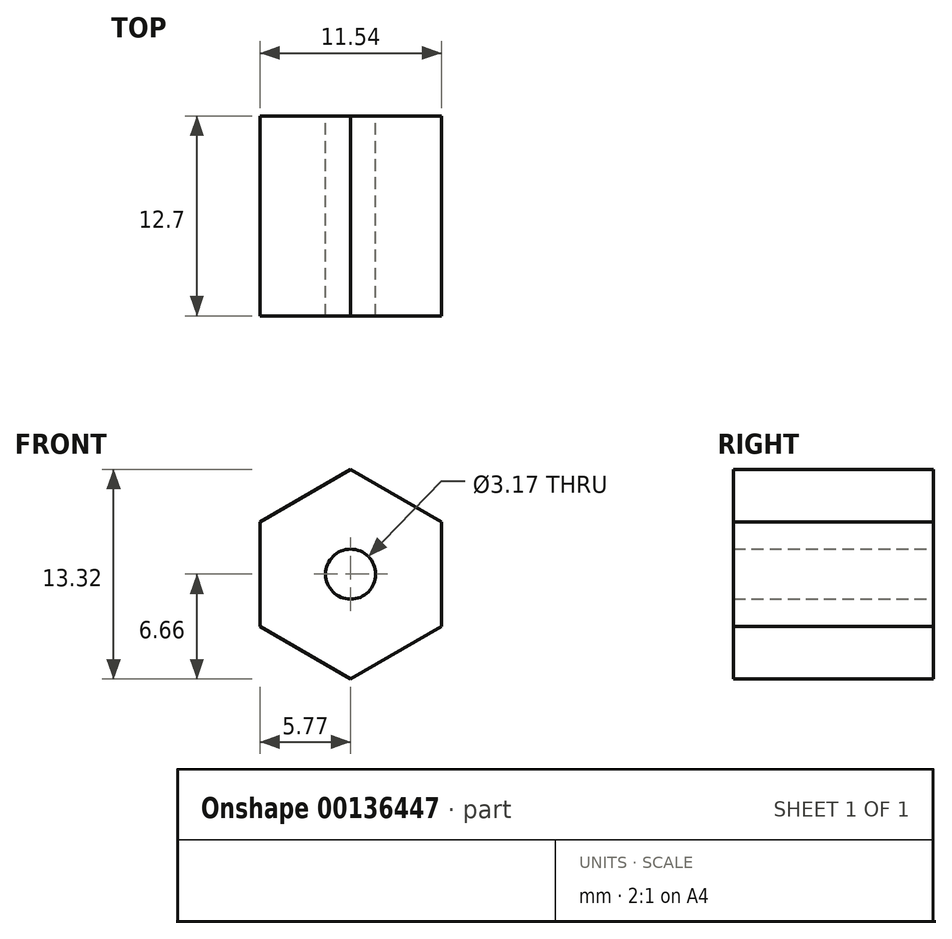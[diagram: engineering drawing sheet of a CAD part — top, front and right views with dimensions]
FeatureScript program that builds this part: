
annotation { "Feature Type Name" : "Feature", "Feature Type Description" : "" }
export const myFeature = defineFeature(function(context is Context, id is Id, definition is map)
    precondition{}
    {
        {
            var Q0;
            Q0=qCreatedBy(makeId("Front.planeOp"),FACE);
            var sketch = newSketch(context, id + "F0", { "sketchPlane" : qUnion([Q0])});
            skLineSegment(sketch, "E0", {"start": v(0, 0) * mm, "end": v(0, 6.66) * mm});
            skPoint(sketch, "E1.center", {"position": v(0, 0) * mm});
            skCircle(sketch, "E2", {"center": v(0, 0) * mm, "radius": 1.59 * mm});
            skLineSegment(sketch, "E3.1.0", {"start": v(0, 0) * mm, "end": v(-1.37, 0.8) * mm});
            skLineSegment(sketch, "E3.2.0", {"start": v(0, 0) * mm, "end": v(-1.37, -0.8) * mm});
            skLineSegment(sketch, "E3.3.0", {"start": v(0, 0) * mm, "end": v(0, -1.59) * mm});
            skLineSegment(sketch, "E3.4.0", {"start": v(0, 0) * mm, "end": v(1.37, -0.8) * mm});
            skLineSegment(sketch, "E3.5.0", {"start": v(0, 0) * mm, "end": v(1.37, 0.8) * mm});
            skLineSegment(sketch, "E4", {"start": v(0, 6.66) * mm, "end": v(-5.77, 3.33) * mm});
            skLineSegment(sketch, "E5", {"start": v(-5.77, -3.33) * mm, "end": v(-5.77, 3.33) * mm});
            skLineSegment(sketch, "E6", {"start": v(-5.77, -3.33) * mm, "end": v(0, -6.66) * mm});
            skLineSegment(sketch, "E7", {"start": v(0, -6.66) * mm, "end": v(5.77, -3.33) * mm});
            skLineSegment(sketch, "E8", {"start": v(5.77, -3.33) * mm, "end": v(5.77, 3.33) * mm});
            skLineSegment(sketch, "E9", {"start": v(5.77, 3.33) * mm, "end": v(0, 6.66) * mm});
            skSolve(sketch);
        }
        {
            var Q0;
            {var subQ4=sQuery(id+"F0.wireOp",EDGE,"S9mbtUjo-F72e-0lH4-tHk4-e1tSvo2amQ5F");Q0=makeQuery(id+"F0.imprint","IMPRINT",FACE,{"disambiguationData":[TD([[makeQuery(id+"F0.imprint","IMPRINT",EDGE,{"derivedFrom":subQ4}),1.0]])]});}
            var Q1;
            Q1=makeQuery(id+"F0.imprint","IMPRINT",FACE,{"disambiguationData":[TD([[makeQuery(id+"F0.imprint","IMPRINT",EDGE,{"derivedFrom":sQuery(id+"F0.wireOp",EDGE,"E4")}),1.0]])]});
            extrude(context, id + "F1", {"entities" : qUnion([Q0, Q1]), "depth" : 12.7 * mm});
        }
    });
